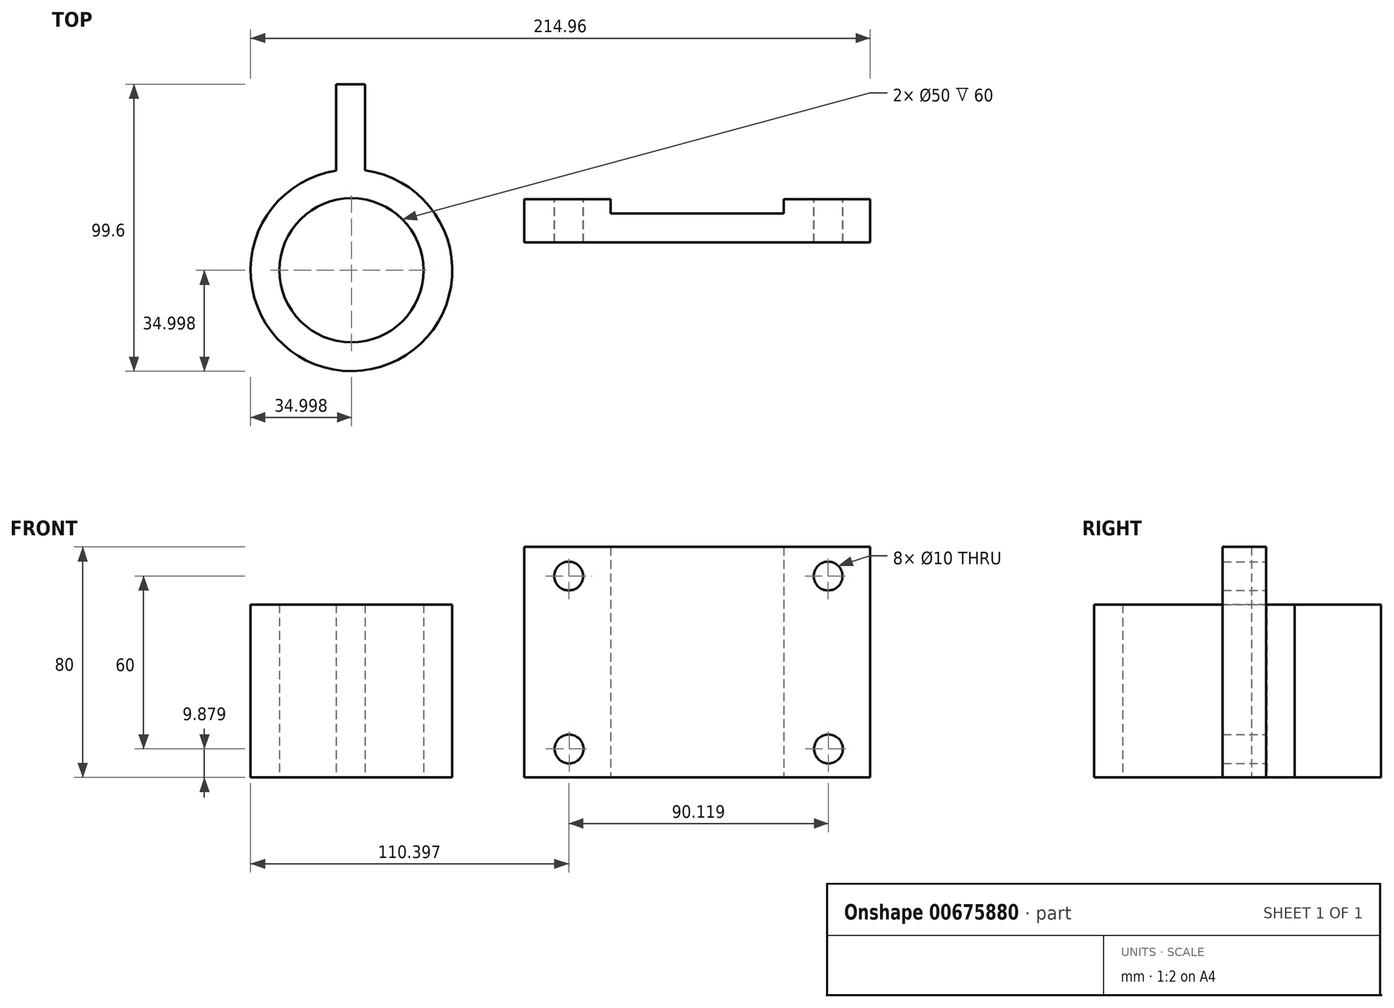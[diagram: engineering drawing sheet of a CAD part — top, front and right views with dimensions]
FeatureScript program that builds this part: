
annotation { "Feature Type Name" : "Feature", "Feature Type Description" : "" }
export const myFeature = defineFeature(function(context is Context, id is Id, definition is map)
    precondition{}
    {
        {
            var Q0;
            Q0=qCreatedBy(makeId("Front.planeOp"),FACE);
            var sketch = newSketch(context, id + "F0", { "sketchPlane" : qUnion([Q0])});
            skLineSegment(sketch, "E0.bottom", {"start": v(0, 0) * mm, "end": v(120, 0) * mm});
            skLineSegment(sketch, "E0.top", {"start": v(0, 80) * mm, "end": v(120, 80) * mm});
            skLineSegment(sketch, "E0.left", {"start": v(0, 0) * mm, "end": v(0, 80) * mm});
            skLineSegment(sketch, "E0.right", {"start": v(120, 0) * mm, "end": v(120, 80) * mm});
            skCircle(sketch, "E1", {"center": v(15.44, 69.88) * mm, "radius": 5 * mm});
            skCircle(sketch, "E2.1.0.0", {"center": v(105.44, 69.88) * mm, "radius": 5 * mm});
            skLineSegment(sketch, "E2.direction1", {"start": v(15.44, 69.88) * mm, "end": v(105.44, 69.88) * mm, "construction": true});
            skCircle(sketch, "E3", {"center": v(15.56, 9.88) * mm, "radius": 5 * mm});
            skCircle(sketch, "E4.1.0.0", {"center": v(105.56, 9.88) * mm, "radius": 5 * mm});
            skCircle(sketch, "E4.2.0.0", {"center": v(195.56, 9.88) * mm, "radius": 5 * mm});
            skLineSegment(sketch, "E4.direction1", {"start": v(15.56, 9.88) * mm, "end": v(105.56, 9.88) * mm, "construction": true});
            skSolve(sketch);
        }
        {
            var Q0;
            Q0 = qSketchRegion(id + "F0", true);
            extrude(context, id + "F1", {"entities" : qUnion([Q0]), "depth" : 15 * mm, "offsetDistance" : 25 * mm});
        }
        {
            var Q0;
            Q0=makeQuery(id+"F1.opExtrude","SWEPT_BODY",BODY,{"disambiguationData":[OSD([sQuery(id+"F0.wireOp",EDGE,"E4.2.0.0")])]});
            deleteBodies(context, id + "F2", {"entities" : qUnion([Q0])});
        }
        {
            var Q0;
            Q0=qCreatedBy(makeId("Top.planeOp"),FACE);
            var sketch = newSketch(context, id + "F3", { "sketchPlane" : qUnion([Q0])});
            skLineSegment(sketch, "E5.bottom", {"start": v(30, 0) * mm, "end": v(90, 0) * mm});
            skLineSegment(sketch, "E5.top", {"start": v(30, -5) * mm, "end": v(90, -5) * mm});
            skLineSegment(sketch, "E5.left", {"start": v(30, 0) * mm, "end": v(30, -5) * mm});
            skLineSegment(sketch, "E5.right", {"start": v(90, 0) * mm, "end": v(90, -5) * mm});
            skSolve(sketch);
        }
        {
            var Q0;
            Q0 = qSketchRegion(id + "F3", true);
            extrude(context, id + "F4", {"entities" : qUnion([Q0]), "operationType" : NewBodyOperationType.REMOVE, "depth" : 120 * mm, "offsetDistance" : 25 * mm});
        }
        {
            var Q0;
            Q0=qCreatedBy(makeId("Front.planeOp"),FACE);
            var sketch = newSketch(context, id + "F5", { "sketchPlane" : qUnion([Q0])});
            skLineSegment(sketch, "E6.bottom", {"start": v(90, 75) * mm, "end": v(80, 75) * mm});
            skLineSegment(sketch, "E6.top", {"start": v(90, 4.99) * mm, "end": v(80, 4.99) * mm});
            skLineSegment(sketch, "E6.left", {"start": v(90, 75) * mm, "end": v(90, 4.99) * mm});
            skLineSegment(sketch, "E6.right", {"start": v(80, 75) * mm, "end": v(80, 4.99) * mm});
            skSolve(sketch);
        }
        {
            var Q0;
            Q0 = qSketchRegion(id + "F5", true);
            var Q1;
            Q1=makeQuery(id+"F1.opExtrude","CAP_FACE",FACE,{"disambiguationData":[OSD([sQuery(id+"F0.wireOp",EDGE,"E0.bottom"),sQuery(id+"F0.wireOp",EDGE,"E0.top"),sQuery(id+"F0.wireOp",EDGE,"E0.left"),sQuery(id+"F0.wireOp",EDGE,"E0.right"),sQuery(id+"F0.wireOp",EDGE,"E1"),sQuery(id+"F0.wireOp",EDGE,"E2.1.0.0"),sQuery(id+"F0.wireOp",EDGE,"E3"),sQuery(id+"F0.wireOp",EDGE,"E4.1.0.0")])],"isStart":false});
            extrude(context, id + "F6", {"entities" : qUnion([Q0]), "depth" : 40 * mm, "endBoundEntityFace" : qUnion([Q1]), "offsetDistance" : 25 * mm});
        }
        {
            var Q0;
            Q0=qCreatedBy(makeId("Top.planeOp"),FACE);
            var sketch = newSketch(context, id + "F7", { "sketchPlane" : qUnion([Q0])});
            skLineSegment(sketch, "E7.bottom", {"start": v(79.99, -5) * mm, "end": v(90, -5) * mm});
            skLineSegment(sketch, "E7.top", {"start": v(79.99, 0) * mm, "end": v(90, 0) * mm});
            skLineSegment(sketch, "E7.left", {"start": v(79.99, -5) * mm, "end": v(79.99, 0) * mm});
            skLineSegment(sketch, "E7.right", {"start": v(90, -5) * mm, "end": v(90, 0) * mm});
            skSolve(sketch);
        }
        {
            var Q0;
            Q0 = qSketchRegion(id + "F7", true);
            extrude(context, id + "F8", {"entities" : qUnion([Q0]), "operationType" : NewBodyOperationType.REMOVE, "oppositeDirection" : true, "depth" : 90 * mm, "offsetDistance" : 25 * mm});
        }
        {
            var Q0;
            Q0=makeQuery(id+"F6.opExtrude","SWEPT_BODY",BODY,{"disambiguationData":[OSD([sQuery(id+"F5.wireOp",EDGE,"E6.bottom"),sQuery(id+"F5.wireOp",EDGE,"E6.top"),sQuery(id+"F5.wireOp",EDGE,"E6.left"),sQuery(id+"F5.wireOp",EDGE,"E6.right")])]});
            deleteBodies(context, id + "F9", {"entities" : qUnion([Q0])});
        }
        {
            var Q0;
            Q0=qCreatedBy(makeId("Top.planeOp"),FACE);
            var sketch = newSketch(context, id + "F10", { "sketchPlane" : qUnion([Q0])});
            skCircle(sketch, "E8", {"center": v(-59.96, -24.7) * mm, "radius": 35 * mm});
            skCircle(sketch, "E9", {"center": v(-59.96, -24.7) * mm, "radius": 25 * mm});
            skLineSegment(sketch, "E10.bottom", {"start": v(-65.23, 9.9) * mm, "end": v(-55.23, 9.9) * mm});
            skLineSegment(sketch, "E10.top", {"start": v(-65.23, 39.9) * mm, "end": v(-55.23, 39.9) * mm});
            skLineSegment(sketch, "E10.left", {"start": v(-65.23, 9.9) * mm, "end": v(-65.23, 39.9) * mm});
            skLineSegment(sketch, "E10.right", {"start": v(-55.23, 9.9) * mm, "end": v(-55.23, 39.9) * mm});
            skSolve(sketch);
        }
        {
            var Q0;
            Q0 = qSketchRegion(id + "F10", true);
            extrude(context, id + "F11", {"entities" : qUnion([Q0]), "depth" : 60 * mm, "offsetDistance" : 25 * mm});
        }
    });
